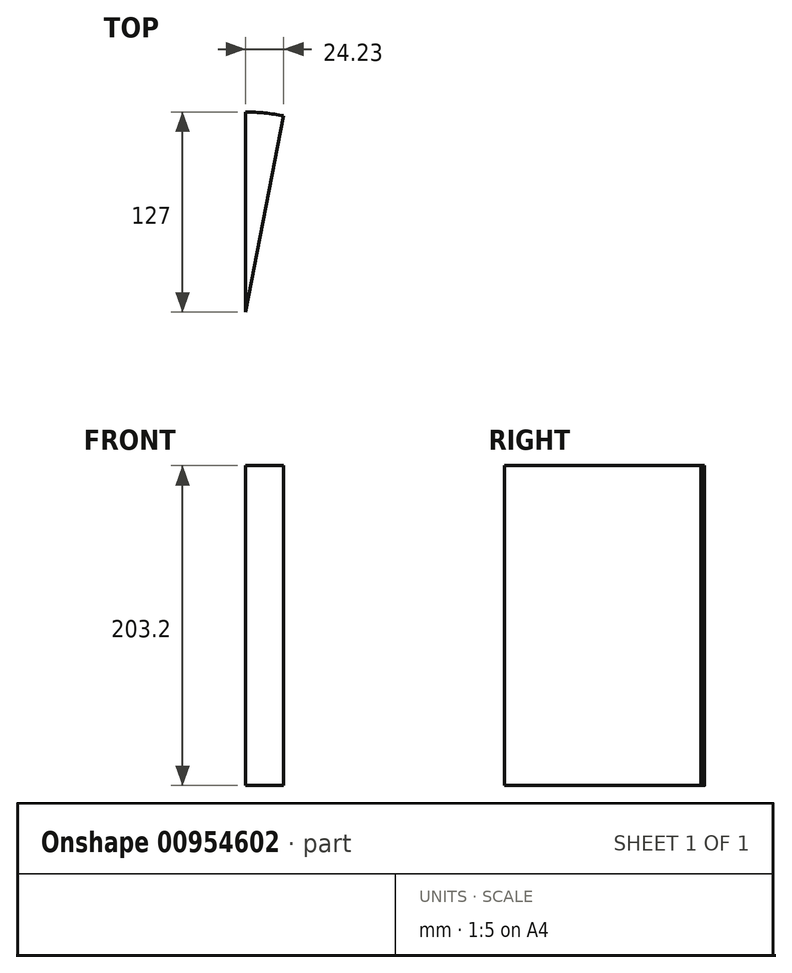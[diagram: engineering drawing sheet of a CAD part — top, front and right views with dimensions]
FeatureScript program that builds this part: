
annotation { "Feature Type Name" : "Feature", "Feature Type Description" : "" }
export const myFeature = defineFeature(function(context is Context, id is Id, definition is map)
    precondition{}
    {
        {
            var Q0;
            Q0=qCreatedBy(makeId("Top.planeOp"),FACE);
            var sketch = newSketch(context, id + "F0", { "sketchPlane" : qUnion([Q0])});
            skCircle(sketch, "E0", {"center": v(0, 0) * mm, "radius": 127 * mm});
            skSolve(sketch);
        }
        {
            var Q0;
            Q0=makeQuery(id+"F0.imprint","IMPRINT",FACE,{"disambiguationData":[TD([[makeQuery(id+"F0.imprint","IMPRINT",EDGE,{"derivedFrom":sQuery(id+"F0.wireOp",EDGE,"E0")}),1.0]])]});
            var sketch = newSketch(context, id + "F1", { "sketchPlane" : qUnion([Q0])});
            skLineSegment(sketch, "E1", {"start": v(0, 0) * mm, "end": v(0, 127) * mm});
            skLineSegment(sketch, "E2", {"start": v(24.23, 124.67) * mm, "end": v(0, 0) * mm});
            skArc(sketch, "E3.0", {"start": v(24.23, 124.67) * mm, "mid": v(12.17, 126.42) * mm, "end": v(0, 127) * mm});
            skSolve(sketch);
        }
        {
            var Q0;
            Q0 = qSketchRegion(id + "F1", true);
            extrude(context, id + "F2", {"entities" : qUnion([Q0]), "depth" : 203.2 * mm, "offsetDistance" : 25.4 * mm});
        }
    });
